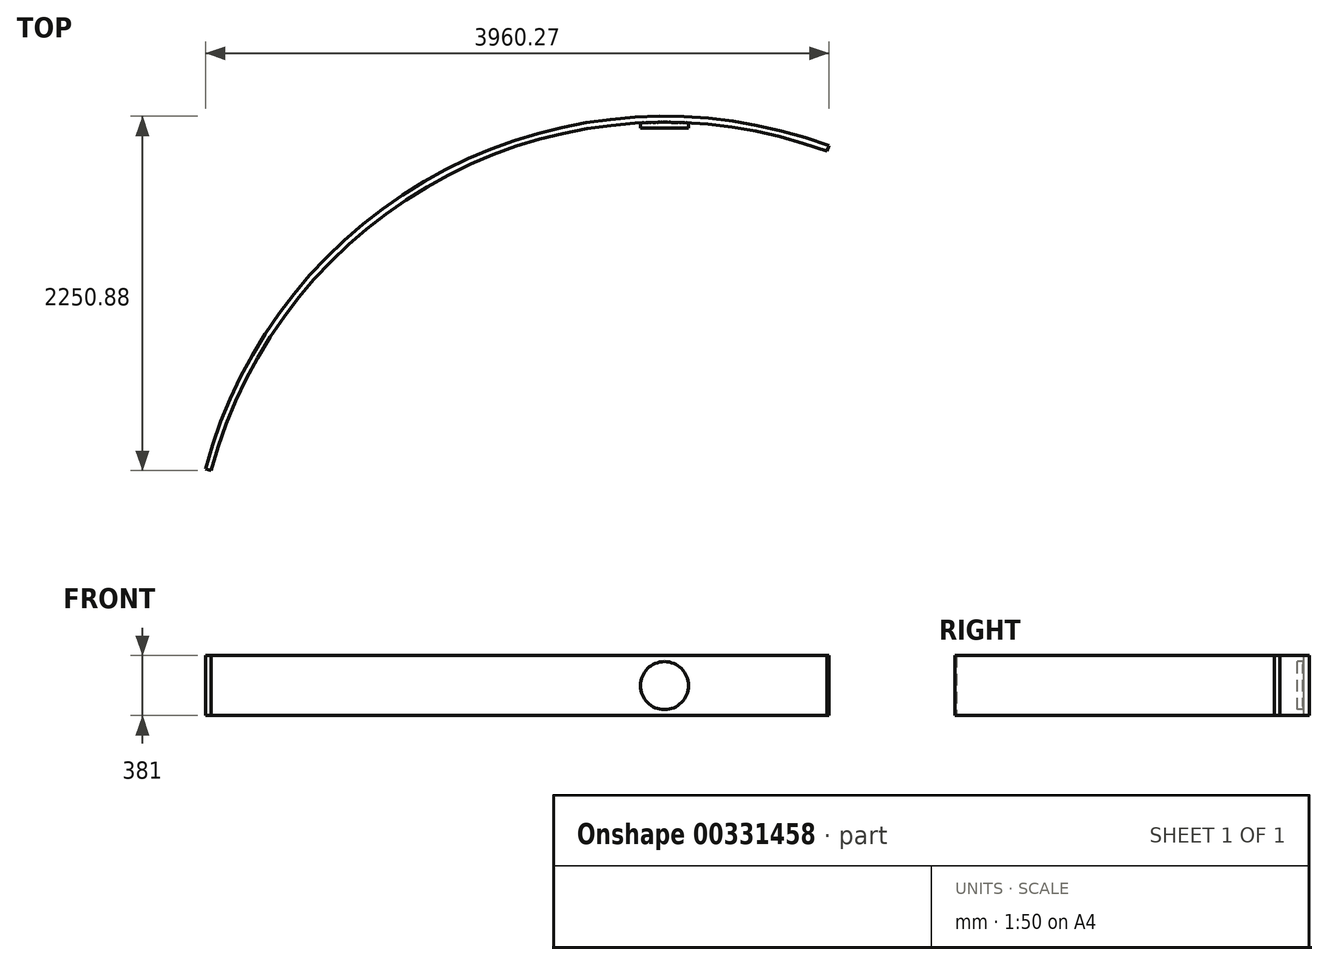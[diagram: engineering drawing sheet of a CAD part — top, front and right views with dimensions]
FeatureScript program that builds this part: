
annotation { "Feature Type Name" : "Feature", "Feature Type Description" : "" }
export const myFeature = defineFeature(function(context is Context, id is Id, definition is map)
    precondition{}
    {
        {
            var Q0;
            Q0=qCreatedBy(makeId("Top.planeOp"),FACE);
            var sketch = newSketch(context, id + "F0", { "sketchPlane" : qUnion([Q0])});
            skArc(sketch, "E0", {"start": v(1044.36, 2831.03) * mm, "mid": v(-1389.6, 2678.51) * mm, "end": v(-2915.91, 776.45) * mm});
            skArc(sketch, "E1.0", {"start": v(1031.17, 2795.29) * mm, "mid": v(-1372.06, 2644.7) * mm, "end": v(-2879.1, 766.64) * mm});
            skLineSegment(sketch, "E2", {"start": v(1031.17, 2795.29) * mm, "end": v(1044.36, 2831.03) * mm});
            skLineSegment(sketch, "E3", {"start": v(-2915.91, 776.45) * mm, "end": v(-2879.1, 766.64) * mm});
            skSolve(sketch);
        }
        {
            var Q0;
            Q0=qCreatedBy(makeId("Front.planeOp"),FACE);
            cPlane(context, id + "F1", {"entities" : qUnion([Q0]), "cplaneType" : CPlaneType.OFFSET, "offset" : 2941.32 * mm, "oppositeDirection" : true, "width" : 152.4 * mm, "height" : 152.4 * mm});
        }
        {
            var Q0;
            Q0 = qSketchRegion(id + "F0", true);
            extrude(context, id + "F2", {"entities" : qUnion([Q0]), "depth" : 381 * mm, "offsetDistance" : 30.48 * mm, "symmetric" : true});
        }
        {
            var Q0;
            Q0=qCreatedBy(id+"F1.planeOp",FACE);
            var sketch = newSketch(context, id + "F3", { "sketchPlane" : qUnion([Q0])});
            skCircle(sketch, "E4", {"center": v(0, 0) * mm, "radius": 152.4 * mm});
            skSolve(sketch);
        }
        {
            var Q0;
            Q0=makeQuery(id+"F3.imprint","IMPRINT",FACE,{"disambiguationData":[TD([[makeQuery(id+"F3.imprint","IMPRINT",EDGE,{"derivedFrom":sQuery(id+"F3.wireOp",EDGE,"E4")}),1.0]])]});
            extrude(context, id + "F4", {"entities" : qUnion([Q0]), "endBound" : BoundingType.UP_TO_NEXT, "oppositeDirection" : true, "depth" : 30.48 * mm, "offsetDistance" : 30.48 * mm});
        }
    });
